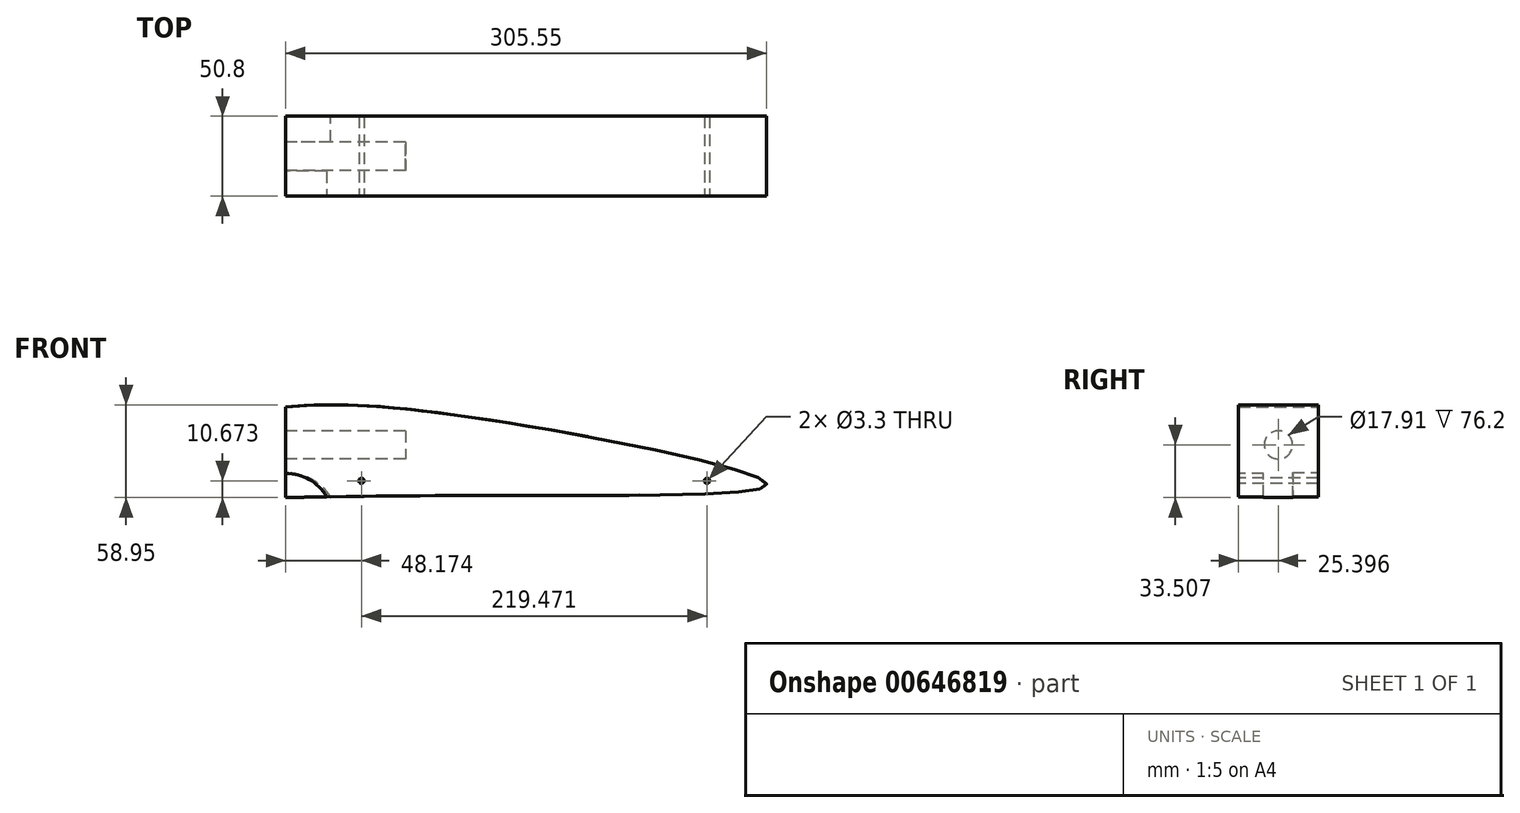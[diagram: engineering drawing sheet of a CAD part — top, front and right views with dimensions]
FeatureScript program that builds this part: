
annotation { "Feature Type Name" : "Feature", "Feature Type Description" : "" }
export const myFeature = defineFeature(function(context is Context, id is Id, definition is map)
    precondition{}
    {
        {
            var Q0;
            Q0=qCreatedBy(makeId("Front.planeOp"),FACE);
            var sketch = newSketch(context, id + "F0", { "sketchPlane" : qUnion([Q0])});
            skLineSegment(sketch, "E0", {"start": v(0, 0) * mm, "end": v(304.8, 0) * mm});
            skLineSegment(sketch, "E1", {"start": v(0, 0) * mm, "end": v(0, 69.09) * mm});
            skLineSegment(sketch, "E2", {"start": v(304.8, 0) * mm, "end": v(304.8, 19.81) * mm});
            skLineSegment(sketch, "E3", {"start": v(304.8, 19.81) * mm, "end": v(0, 69.09) * mm});
            skSolve(sketch);
        }
        {
            var Q0;
            Q0 = qSketchRegion(id + "F0", true);
            extrude(context, id + "F1", {"entities" : qUnion([Q0]), "depth" : 42.16 * mm, "offsetDistance" : 25.4 * mm});
        }
        {
            var Q0;
            Q0=makeQuery(id+"F1.opExtrude","CAP_FACE",FACE,{"disambiguationData":[OSD([sQuery(id+"F0.wireOp",EDGE,"E0"),sQuery(id+"F0.wireOp",EDGE,"E1"),sQuery(id+"F0.wireOp",EDGE,"E2"),sQuery(id+"F0.wireOp",EDGE,"E3")])],"isStart":false});
            var sketch = newSketch(context, id + "F2", { "sketchPlane" : qUnion([Q0])});
            skFitSpline(sketch, "E4", {"points": [v(0, 57.71) * mm, v(85.3, 55.3) * mm, v(304.8, 9.9) * mm, v(0, 0) * mm], "startDerivative": vector(274.87, 17.7) * mm, "endDerivative": vector(-1151.08, -27) * mm});
            skLineSegment(sketch, "E5", {"start": v(0, 57.71) * mm, "end": v(0, 0) * mm});
            skSolve(sketch);
        }
        {
            var Q0;
            Q0 = qSketchRegion(id + "F2", true);
            extrude(context, id + "F3", {"entities" : qUnion([Q0]), "depth" : 50.8 * mm, "offsetDistance" : 25.4 * mm});
        }
        {
            var Q0;
            Q0=makeQuery(id+"F1.opExtrude","SWEPT_BODY",BODY,{"disambiguationData":[OSD([sQuery(id+"F0.wireOp",EDGE,"E0"),sQuery(id+"F0.wireOp",EDGE,"E1"),sQuery(id+"F0.wireOp",EDGE,"E2"),sQuery(id+"F0.wireOp",EDGE,"E3")])]});
            deleteBodies(context, id + "F4", {"entities" : qUnion([Q0])});
        }
        {
            var Q0;
            Q0=makeQuery(id+"F3.opExtrude","SWEPT_FACE",FACE,{"disambiguationData":[OSD([sQuery(id+"F2.wireOp",EDGE,"E5")])]});
            var sketch = newSketch(context, id + "F5", { "sketchPlane" : qUnion([Q0])});
            skCircle(sketch, "E6", {"center": v(67.56, 33.5) * mm, "radius": 8.96 * mm});
            skPoint(sketch, "E6.centerSnap0", {"position": v(67.56, 57.71) * mm});
            skSolve(sketch);
        }
        {
            var Q0;
            Q0 = qSketchRegion(id + "F5", true);
            extrude(context, id + "F6", {"entities" : qUnion([Q0]), "operationType" : NewBodyOperationType.REMOVE, "oppositeDirection" : true, "depth" : 76.2 * mm, "offsetDistance" : 25.4 * mm});
        }
        {
            var Q0;
            Q0=makeQuery(id+"F3.opExtrude","CAP_FACE",FACE,{"disambiguationData":[OSD([sQuery(id+"F2.wireOp",EDGE,"E4"),sQuery(id+"F2.wireOp",EDGE,"E5")])],"isStart":false});
            var sketch = newSketch(context, id + "F7", { "sketchPlane" : qUnion([Q0])});
            skArc(sketch, "E7", {"start": v(26, 0.52) * mm, "mid": v(15.07, 11.53) * mm, "end": v(0, 15.2) * mm});
            skLineSegment(sketch, "E8", {"start": v(0, 15.2) * mm, "end": v(0, 0) * mm});
            skLineSegment(sketch, "E9", {"start": v(0, 0) * mm, "end": v(26, 0.52) * mm});
            skArc(sketch, "E10", {"start": v(26, 0.52) * mm, "mid": v(14.92, 11.27) * mm, "end": v(0, 15.2) * mm});
            skLineSegment(sketch, "E11", {"start": v(26, 0.52) * mm, "end": v(0, 0) * mm});
            skSolve(sketch);
        }
        {
            var Q0;
            Q0 = qSketchRegion(id + "F7", true);
            extrude(context, id + "F8", {"entities" : qUnion([Q0]), "operationType" : NewBodyOperationType.REMOVE, "oppositeDirection" : true, "depth" : 16 * mm, "offsetDistance" : 25.4 * mm});
        }
        {
            var Q0;
            Q0=makeQuery(id+"F3.opExtrude","CAP_FACE",FACE,{"disambiguationData":[OSD([sQuery(id+"F2.wireOp",EDGE,"E4"),sQuery(id+"F2.wireOp",EDGE,"E5")])],"isStart":true});
            var sketch = newSketch(context, id + "F9", { "sketchPlane" : qUnion([Q0])});
            skArc(sketch, "E12", {"start": v(0, 15.9) * mm, "mid": v(-16.2, 11.7) * mm, "end": v(-28.69, 0.57) * mm});
            skLineSegment(sketch, "E13", {"start": v(-28.69, 0.57) * mm, "end": v(0, 0) * mm});
            skLineSegment(sketch, "E14", {"start": v(0, 0) * mm, "end": v(0, 15.9) * mm});
            skSolve(sketch);
        }
        {
            var Q0;
            Q0 = qSketchRegion(id + "F9", true);
            extrude(context, id + "F10", {"entities" : qUnion([Q0]), "operationType" : NewBodyOperationType.REMOVE, "oppositeDirection" : true, "depth" : 16.26 * mm, "offsetDistance" : 25.4 * mm});
        }
        {
            var Q0;
            Q0=makeQuery(id+"F3.opExtrude","CAP_FACE",FACE,{"disambiguationData":[OSD([sQuery(id+"F2.wireOp",EDGE,"E4"),sQuery(id+"F2.wireOp",EDGE,"E5")])],"isStart":false});
            var sketch = newSketch(context, id + "F11", { "sketchPlane" : qUnion([Q0])});
            skCircle(sketch, "E15", {"center": v(48.17, 10.67) * mm, "radius": 1.65 * mm});
            skCircle(sketch, "E16", {"center": v(267.64, 10.67) * mm, "radius": 1.65 * mm});
            skSolve(sketch);
        }
        {
            var Q0;
            Q0 = qSketchRegion(id + "F11", true);
            extrude(context, id + "F12", {"entities" : qUnion([Q0]), "operationType" : NewBodyOperationType.REMOVE, "oppositeDirection" : true, "depth" : 59.94 * mm, "offsetDistance" : 25.4 * mm});
        }
        {
            var Q0;
            Q0 = qSketchRegion(id + "F11", true);
            extrude(context, id + "F13", {"entities" : qUnion([Q0]), "operationType" : NewBodyOperationType.REMOVE, "oppositeDirection" : true, "depth" : 89.92 * mm, "offsetDistance" : 25.4 * mm});
        }
    });
